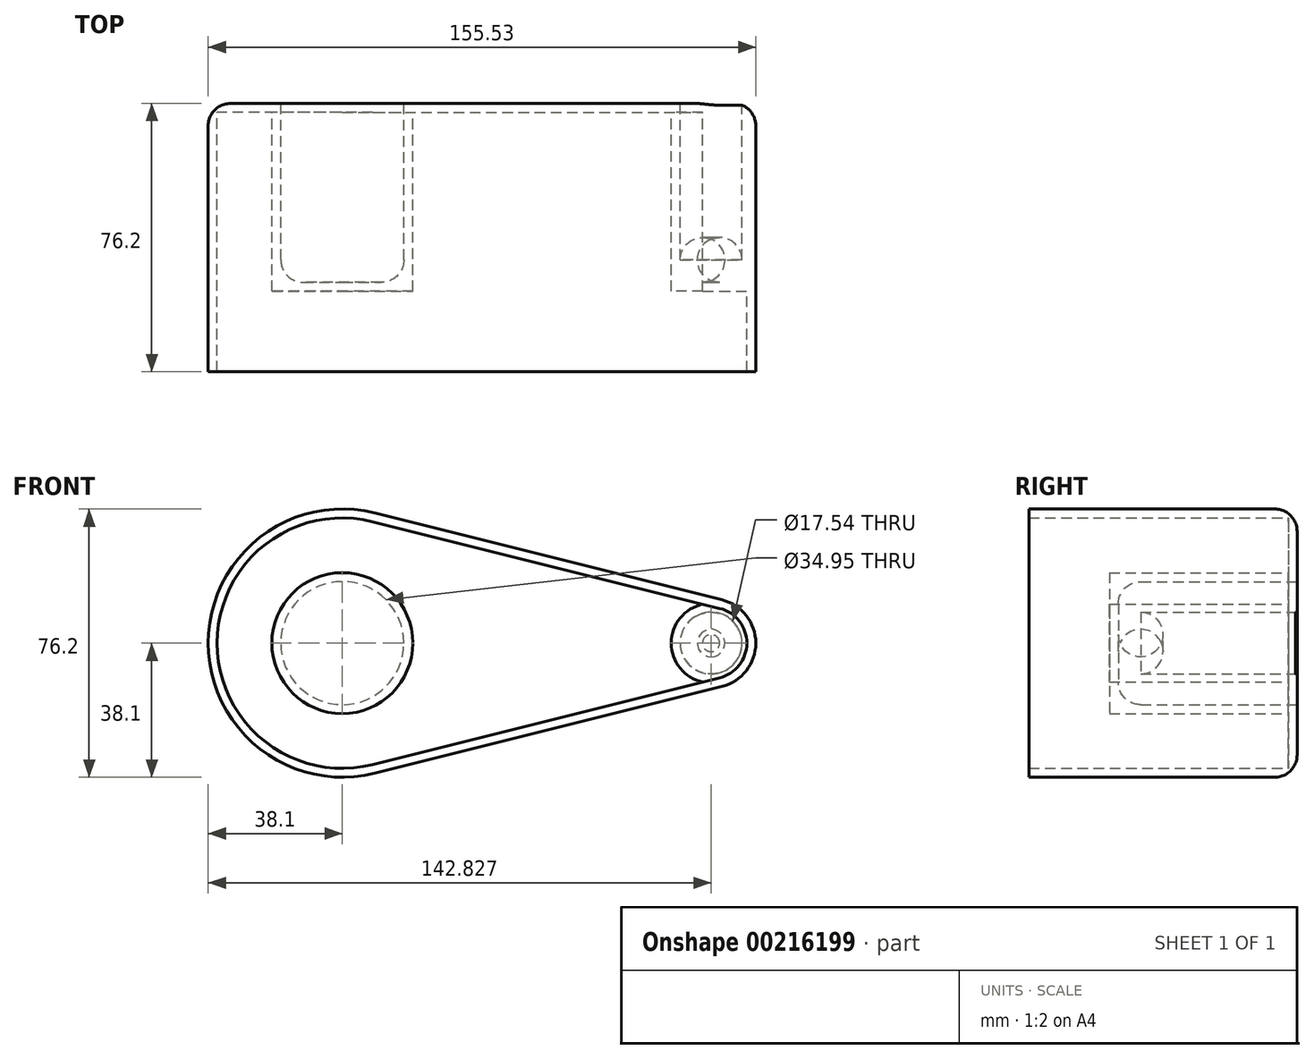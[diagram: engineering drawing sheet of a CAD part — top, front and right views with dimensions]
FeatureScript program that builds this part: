
annotation { "Feature Type Name" : "Feature", "Feature Type Description" : "" }
export const myFeature = defineFeature(function(context is Context, id is Id, definition is map)
    precondition{}
    {
        {
            var Q0;
            Q0=qCreatedBy(makeId("Front.planeOp"),FACE);
            var sketch = newSketch(context, id + "F0", { "sketchPlane" : qUnion([Q0])});
            skCircle(sketch, "E0", {"center": v(0, 0) * mm, "radius": 38.1 * mm});
            skCircle(sketch, "E1", {"center": v(104.73, 0) * mm, "radius": 12.7 * mm});
            skLineSegment(sketch, "E2", {"start": v(9.24, 36.96) * mm, "end": v(107.8, 12.32) * mm});
            skLineSegment(sketch, "E3", {"start": v(9.24, -36.96) * mm, "end": v(107.8, -12.32) * mm});
            skSolve(sketch);
        }
        {
            var Q0;
            Q0 = qSketchRegion(id + "F0", true);
            extrude(context, id + "F1", {"entities" : qUnion([Q0]), "depth" : 76.2 * mm});
        }
        {
            var Q0;
            Q0=makeQuery(id+"F1.opExtrude","CAP_FACE",FACE,{"disambiguationData":[OSD([sQuery(id+"F0.wireOp",EDGE,"E0"),sQuery(id+"F0.wireOp",EDGE,"E1"),sQuery(id+"F0.wireOp",EDGE,"E2"),sQuery(id+"F0.wireOp",EDGE,"E3")])],"isStart":true});
            var sketch = newSketch(context, id + "F2", { "sketchPlane" : qUnion([Q0])});
            skCircle(sketch, "E4", {"center": v(0, 0) * mm, "radius": 17.47 * mm});
            skCircle(sketch, "E5", {"center": v(-104.73, 0) * mm, "radius": 8.77 * mm});
            skSolve(sketch);
        }
        {
            var Q0;
            Q0 = qSketchRegion(id + "F2", true);
            extrude(context, id + "F3", {"entities" : qUnion([Q0]), "operationType" : NewBodyOperationType.REMOVE, "oppositeDirection" : true, "depth" : 50.8 * mm});
        }
        {
            var Q0;
            Q0=makeQuery(id+"F1.opExtrude","CAP_FACE",FACE,{"disambiguationData":[OSD([sQuery(id+"F0.wireOp",EDGE,"E0"),sQuery(id+"F0.wireOp",EDGE,"E1"),sQuery(id+"F0.wireOp",EDGE,"E2"),sQuery(id+"F0.wireOp",EDGE,"E3")])],"isStart":false});
            shell(context, id + "F4", {"entities" : qUnion([Q0]), "thickness" : 2.54 * mm});
        }
        {
            var Q0;
            Q0=makeQuery(id+"F3.boolean.opBoolean","COPY",EDGE,{"derivedFrom":makeQuery(id+"F3.opExtrude","CAP_EDGE",EDGE,{"disambiguationData":[OSD([sQuery(id+"F2.wireOp",EDGE,"E5")])],"isStart":false})});
            var Q1;
            Q1=makeQuery(id+"F3.boolean.opBoolean","COPY",EDGE,{"derivedFrom":makeQuery(id+"F3.opExtrude","CAP_EDGE",EDGE,{"disambiguationData":[OSD([sQuery(id+"F2.wireOp",EDGE,"E4")])],"isStart":false})});
            var Q2;
            Q2=makeQuery(id+"F3.boolean.opBoolean","COPY",EDGE,{"derivedFrom":makeQuery(id+"F3.opExtrude","CAP_EDGE",EDGE,{"disambiguationData":[OSD([sQuery(id+"F2.wireOp",EDGE,"E5")])],"isStart":true})});
            var Q3;
            Q3=makeQuery(id+"F3.boolean.opBoolean","COPY",EDGE,{"derivedFrom":makeQuery(id+"F3.opExtrude","CAP_EDGE",EDGE,{"disambiguationData":[OSD([sQuery(id+"F2.wireOp",EDGE,"E4")])],"isStart":true})});
            var Q4;
            Q4=makeQuery(id+"F1.opExtrude","CAP_EDGE",EDGE,{"disambiguationData":[OSD([sQuery(id+"F0.wireOp",EDGE,"E2")])],"isStart":true});
            fillet(context, id + "F5", {"entities" : qUnion([Q0, Q1, Q2, Q3, Q4]), "radius" : 6.35 * mm, "tangentPropagation" : true, "allowEdgeOverflow" : false});
        }
    });
